# Revit family: CBKLEDS-BLK_non hosted R16
name_source: partatom
category: Lighting Fixtures
revit_build: Autodesk Revit LT 2016 (Build: 20150220_1215(x64)
units: mm (PartAtom-declared; Revit-internal decimal feet)

## family parameters
Always vertical = Yes
Cut with Voids When Loaded = No
Light Source = Yes
OmniClass Number = 23.80.70.00
OmniClass Title = Lighting
Part Type = Normal
Room Calculation Point = No
Round Connector Dimension = Use Diameter
Shared = No
Work Plane-Based = No

## types (2) — shared parameters
AS2293 Classification = C0=D25 C90=D25
Catalogue Number = CBKLEDS-BLK
Color Filter = 16777215
Construction = Base Material: Die-cast aluminium
Diffuser Cover Material: Opal polycarbonate
Description = LP Premium Bunkalite IP65 Weatherproof emergency luminaire, black
Dimensions L x W x H = Diamater 360mm, Depth 145mm
Dimming Lamp Color Temperature Shift = <None>
IP Rating = IP65
Impact Rating = IK10
LED Driver = Constant current, 500mA, 50,000hrs
Lamp = LED module, 4,000K natural white, 50,000h life, Ra>80
Mounting = Surface mount
Operating Mode = Sustained
Operating Temperature = 0˚C to 40˚C
Operating Voltage = 240V AC; 50Hz
Photometric Web File = 698_CBKLEDS-BLK_Dali_Tridonics_EmergencyMode_08022017-02_IES2002_Revised.ies
Power Factor = 0.9
Tilt Angle = 90.00°
Total lumen output = 1400 lm @ 82lm/W (87lm/W non-emergency version)

## per-type parameters (varying)
| type | Charging Method | Power Consumption | Testing System |
| FBKLED |  | 17 Watts (lamps ON), |  |
| CBKLED | Intelligent Current Limited Constant Voltage | 17 Watts (lamps ON), 1.0 Watts (lamp OFF) | N/A - Manual test switch |

## geometry (parser evidence)
native form markers: Sweep x2
no freeform markers — native parametric forms only
